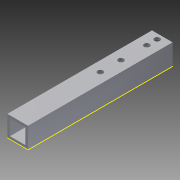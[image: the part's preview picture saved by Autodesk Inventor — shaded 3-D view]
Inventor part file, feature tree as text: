
AUTODESK INVENTOR PART (.ipt)
format: ipt  version: 2013 (Build 170138000, 138)  size: 115,200 bytes
history: native  units: in
note: dims shown in document units (in); Inventor stores cm internally (conversion verified against a paired STEP export)
features: reference x7, extrude x4, sketch x4
ambient origin geometry x8: Origin, YZ Plane, XZ Plane, XY Plane, X Axis, Y Axis, Z Axis, Center Point
bodies: Solid1 (feature_tree)
feature tree (15):
  extrude  "Extrusion1"  Depth=1.0in
  extrude  "Extrusion2"  Depth=7.0in TaperAngle=0.0deg
  extrude  "Extrusion3"  Depth=1.0in TaperAngle=0.0deg
  extrude  "Extrusion4"  [1 undecoded]
  sketch  "Sketch1"  dims[d0=1.0in d2=1.0in]
  sketch  "Sketch2"  dims[d3=0.125in d4=7.0in d5=0.0in]
  reference  "Reference1"
  reference  "Reference2"
  sketch  "Sketch3"  dims[d6=1.0in d7=0.0in d8=1.0in d9=0.0in]
  reference  "Reference3"
  reference  "Reference4"
  reference  "Reference5"
  sketch  "Sketch5"  dims[d10=1.0in d11=0.0in]
  reference  "Reference6"
  reference  "Reference7"
note: 1 required parameter value undecoded (feature->parameter linkage not recoverable at this tier; creation-order binding heuristic only, values carry confidence <= 0.55)
